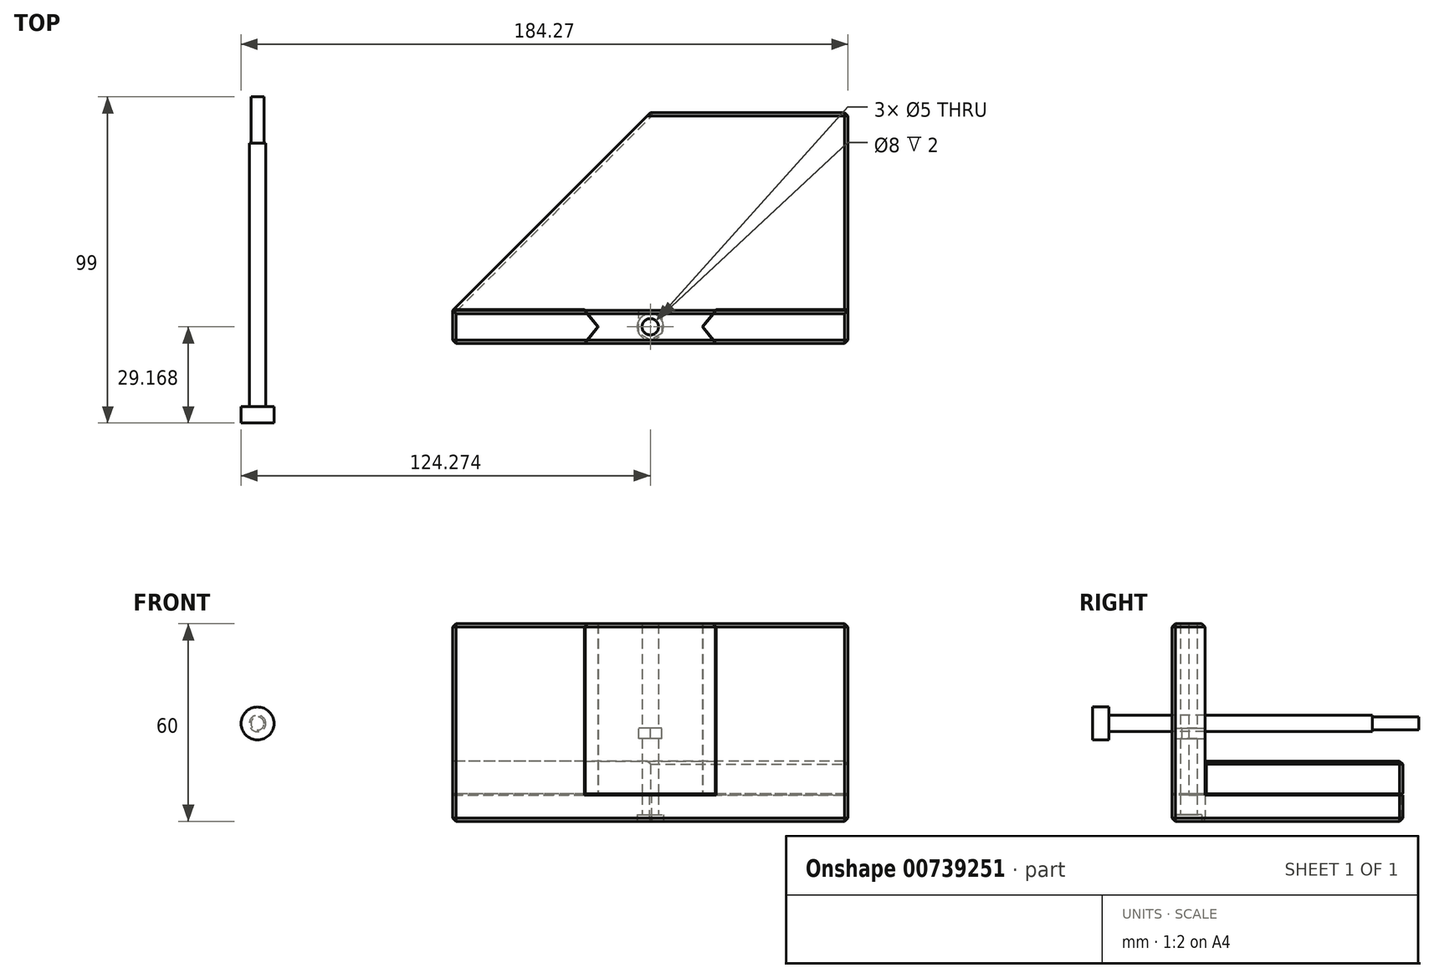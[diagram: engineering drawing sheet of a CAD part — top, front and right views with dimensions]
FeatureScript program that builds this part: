
annotation { "Feature Type Name" : "Feature", "Feature Type Description" : "" }
export const myFeature = defineFeature(function(context is Context, id is Id, definition is map)
    precondition{}
    {
        {
            var Q0;
            Q0=qCreatedBy(makeId("Top.planeOp"),FACE);
            var sketch = newSketch(context, id + "F0", { "sketchPlane" : qUnion([Q0])});
            skLineSegment(sketch, "E0", {"start": v(72.15, 89.17) * mm, "end": v(72.15, 29.17) * mm});
            skLineSegment(sketch, "E1", {"start": v(72.15, 29.17) * mm, "end": v(-47.85, 29.17) * mm});
            skLineSegment(sketch, "E2", {"start": v(-47.85, 29.17) * mm, "end": v(12.15, 89.17) * mm});
            skLineSegment(sketch, "E3", {"start": v(12.15, 89.17) * mm, "end": v(72.15, 89.17) * mm});
            skSolve(sketch);
        }
        {
            var Q0;
            Q0=makeQuery(id+"F0.imprint","IMPRINT",FACE,{"disambiguationData":[TD([[makeQuery(id+"F0.imprint","IMPRINT",EDGE,{"derivedFrom":sQuery(id+"F0.wireOp",EDGE,"E0")}),-1.0]])]});
            extrude(context, id + "F1", {"entities" : qUnion([Q0]), "depth" : 8 * mm, "offsetDistance" : 25 * mm});
        }
        {
            var Q0;
            Q0=makeQuery(id+"F1.opExtrude","CAP_FACE",FACE,{"disambiguationData":[OSD([sQuery(id+"F0.wireOp",EDGE,"E0"),sQuery(id+"F0.wireOp",EDGE,"E1"),sQuery(id+"F0.wireOp",EDGE,"E2"),sQuery(id+"F0.wireOp",EDGE,"E3")])],"isStart":false});
            var sketch = newSketch(context, id + "F2", { "sketchPlane" : qUnion([Q0])});
            skLineSegment(sketch, "E4.0", {"start": v(72.15, 29.17) * mm, "end": v(-47.85, 29.17) * mm});
            skLineSegment(sketch, "E5", {"start": v(72.15, 29.17) * mm, "end": v(72.15, 19.17) * mm});
            skLineSegment(sketch, "E6", {"start": v(72.15, 19.17) * mm, "end": v(-47.85, 19.17) * mm});
            skLineSegment(sketch, "E7", {"start": v(-47.85, 19.17) * mm, "end": v(-47.85, 29.17) * mm});
            skLineSegment(sketch, "E8", {"start": v(12.15, 19.17) * mm, "end": v(12.15, 29.17) * mm, "construction": true});
            skLineSegment(sketch, "E9", {"start": v(-7.85, 29.17) * mm, "end": v(-3.8, 24.17) * mm});
            skLineSegment(sketch, "E10", {"start": v(-3.8, 24.17) * mm, "end": v(-7.85, 19.17) * mm});
            skLineSegment(sketch, "E11.MirrorCS", {"start": v(32.15, 29.17) * mm, "end": v(28.1, 24.17) * mm});
            skLineSegment(sketch, "E12.MirrorCS", {"start": v(28.1, 24.17) * mm, "end": v(32.15, 19.17) * mm});
            skLineSegment(sketch, "E13", {"start": v(-7.85, 29.17) * mm, "end": v(-7.85, 19.17) * mm, "construction": true});
            skSolve(sketch);
        }
        {
            var Q0;
            {var subQ1=sQuery(id+"F2.wireOp",EDGE,"E5");Q0=makeQuery(id+"F2.imprint","IMPRINT",FACE,{"disambiguationData":[TD([[makeQuery(id+"F2.imprint","IMPRINT",EDGE,{"derivedFrom":subQ1}),-1.0]])]});}
            var Q1;
            {var subQ1=sQuery(id+"F2.wireOp",EDGE,"E9");Q1=makeQuery(id+"F2.imprint","IMPRINT",FACE,{"disambiguationData":[TD([[makeQuery(id+"F2.imprint","IMPRINT",EDGE,{"derivedFrom":subQ1}),1.0]])]});}
            var Q2;
            {var subQ1=sQuery(id+"F2.wireOp",EDGE,"E7");Q2=makeQuery(id+"F2.imprint","IMPRINT",FACE,{"disambiguationData":[TD([[makeQuery(id+"F2.imprint","IMPRINT",EDGE,{"derivedFrom":subQ1}),-1.0]])]});}
            var Q3;
            Q3=makeQuery(id+"F1.opExtrude","CAP_FACE",FACE,{"disambiguationData":[OSD([sQuery(id+"F0.wireOp",EDGE,"E0"),sQuery(id+"F0.wireOp",EDGE,"E1"),sQuery(id+"F0.wireOp",EDGE,"E2"),sQuery(id+"F0.wireOp",EDGE,"E3")])],"isStart":true});
            extrude(context, id + "F3", {"entities" : qUnion([Q0, Q1, Q2]), "operationType" : NewBodyOperationType.ADD, "endBound" : BoundingType.UP_TO_SURFACE, "oppositeDirection" : true, "depth" : 25 * mm, "endBoundEntityFace" : qUnion([Q3]), "offsetDistance" : 25 * mm});
        }
        {
            var Q0;
            {var subQ1=sQuery(id+"F2.wireOp",EDGE,"E7");Q0=makeQuery(id+"F2.imprint","IMPRINT",FACE,{"disambiguationData":[TD([[makeQuery(id+"F2.imprint","IMPRINT",EDGE,{"derivedFrom":subQ1}),-1.0]])]});}
            var Q1;
            {var subQ1=sQuery(id+"F2.wireOp",EDGE,"E5");Q1=makeQuery(id+"F2.imprint","IMPRINT",FACE,{"disambiguationData":[TD([[makeQuery(id+"F2.imprint","IMPRINT",EDGE,{"derivedFrom":subQ1}),-1.0]])]});}
            extrude(context, id + "F4", {"entities" : qUnion([Q0, Q1]), "operationType" : NewBodyOperationType.ADD, "depth" : 52 * mm, "offsetDistance" : 25 * mm});
        }
        {
            var Q0;
            {var subQ0=makeQuery(id+"F1.opExtrude","CAP_EDGE",EDGE,{"disambiguationData":[OSD([sQuery(id+"F0.wireOp",EDGE,"E0")])],"isStart":false});Q0=makeQuery(id+"F2.imprint","IMPRINT",FACE,{"disambiguationData":[TD([[makeQuery(id+"F2.imprint","IMPRINT",EDGE,{"derivedFrom":subQ0}),-1.0]])]});}
            cPlane(context, id + "F5", {"entities" : qUnion([Q0]), "cplaneType" : CPlaneType.OFFSET, "offset" : 0.3 * mm, "width" : 150 * mm, "height" : 150 * mm});
        }
        {
            var Q0;
            Q0=qCreatedBy(id+"F5.planeOp",FACE);
            var sketch = newSketch(context, id + "F6", { "sketchPlane" : qUnion([Q0])});
            skLineSegment(sketch, "E14.0", {"start": v(12.15, 89.17) * mm, "end": v(72.15, 89.17) * mm});
            skLineSegment(sketch, "E15.0", {"start": v(-47.85, 29.17) * mm, "end": v(12.15, 89.17) * mm});
            skLineSegment(sketch, "E16.0", {"start": v(72.15, 89.17) * mm, "end": v(72.15, 29.17) * mm});
            skLineSegment(sketch, "E17.0", {"start": v(72.15, 29.17) * mm, "end": v(72.15, 19.17) * mm});
            skLineSegment(sketch, "E18.0", {"start": v(-47.85, 19.17) * mm, "end": v(-47.85, 29.17) * mm});
            skLineSegment(sketch, "E19.0", {"start": v(72.15, 19.17) * mm, "end": v(-47.85, 19.17) * mm});
            skLineSegment(sketch, "E20.0", {"start": v(72.15, 29.17) * mm, "end": v(-47.85, 29.17) * mm, "construction": true});
            skLineSegment(sketch, "E21.0", {"start": v(12.15, 19.17) * mm, "end": v(12.15, 29.17) * mm, "construction": true});
            skLineSegment(sketch, "E22.0", {"start": v(-7.85, 29.17) * mm, "end": v(-7.85, 19.17) * mm, "construction": true});
            skLineSegment(sketch, "E23.0", {"start": v(-7.85, 29.17) * mm, "end": v(-3.8, 24.17) * mm, "construction": true});
            skLineSegment(sketch, "E24.0", {"start": v(-3.8, 24.17) * mm, "end": v(-7.85, 19.17) * mm, "construction": true});
            skLineSegment(sketch, "E25.0", {"start": v(32.15, 29.17) * mm, "end": v(28.1, 24.17) * mm, "construction": true});
            skLineSegment(sketch, "E26.0", {"start": v(28.1, 24.17) * mm, "end": v(32.15, 19.17) * mm, "construction": true});
            skLineSegment(sketch, "E27", {"start": v(-47.55, 29.47) * mm, "end": v(72.15, 29.47) * mm});
            skLineSegment(sketch, "E28.0", {"start": v(27.91, 24.17) * mm, "end": v(31.96, 19.17) * mm});
            skLineSegment(sketch, "E28.1", {"start": v(32.2, 29.47) * mm, "end": v(27.91, 24.17) * mm});
            skLineSegment(sketch, "E29.MirrorCS", {"start": v(-7.9, 29.47) * mm, "end": v(-3.6, 24.17) * mm});
            skLineSegment(sketch, "E30.MirrorCS", {"start": v(-3.6, 24.17) * mm, "end": v(-7.65, 19.17) * mm});
            skLineSegment(sketch, "E31", {"start": v(31.96, 29.17) * mm, "end": v(-7.65, 29.17) * mm});
            skSolve(sketch);
        }
        {
            var Q0;
            {var subQ3=sQuery(id+"F6.wireOp",EDGE,"E28.0");Q0=makeQuery(id+"F6.imprint","IMPRINT",FACE,{"disambiguationData":[TD([[makeQuery(id+"F6.imprint","IMPRINT",EDGE,{"derivedFrom":subQ3}),-1.0]])]});}
            var Q1;
            {var subQ5=sQuery(id+"F6.wireOp",EDGE,"E31");Q1=makeQuery(id+"F6.imprint","IMPRINT",FACE,{"disambiguationData":[TD([[makeQuery(id+"F6.imprint","IMPRINT",EDGE,{"derivedFrom":subQ5}),-1.0]])]});}
            var Q2;
            Q2=makeQuery(id+"F4.opExtrude","CAP_FACE",FACE,{"disambiguationData":[OSD([sQuery(id+"F2.wireOp",EDGE,"E4.0"),sQuery(id+"F2.wireOp",EDGE,"E6"),sQuery(id+"F2.wireOp",EDGE,"E7"),sQuery(id+"F2.wireOp",EDGE,"E9"),sQuery(id+"F2.wireOp",EDGE,"E10")])],"isStart":false});
            extrude(context, id + "F7", {"entities" : qUnion([Q0, Q1]), "depth" : 10 * mm, "endBoundEntityFace" : qUnion([Q2]), "offsetDistance" : 25 * mm});
        }
        {
            var Q0;
            Q0=makeQuery(id+"F7.opExtrude","SWEPT_FACE",FACE,{"disambiguationData":[OSD([sQuery(id+"F6.wireOp",EDGE,"E27")])]});
            var sketch = newSketch(context, id + "F8", { "sketchPlane" : qUnion([Q0])});
            skLineSegment(sketch, "E32.0", {"start": v(-72.15, 60) * mm, "end": v(-72.15, 8) * mm, "construction": true});
            skLineSegment(sketch, "E33.0", {"start": v(47.85, 60) * mm, "end": v(47.85, 8) * mm, "construction": true});
            skLineSegment(sketch, "E34.0", {"start": v(7.9, 8.3) * mm, "end": v(-32.2, 8.3) * mm, "construction": true});
            skLineSegment(sketch, "E35", {"start": v(-72.15, 18.3) * mm, "end": v(47.85, 18.3) * mm});
            skLineSegment(sketch, "E36", {"start": v(-72.15, 8.3) * mm, "end": v(47.85, 8.3) * mm});
            skLineSegment(sketch, "E37", {"start": v(-72.15, 8.3) * mm, "end": v(-72.15, 18.3) * mm});
            skLineSegment(sketch, "E38", {"start": v(47.85, 8.3) * mm, "end": v(47.85, 18.3) * mm});
            skSolve(sketch);
        }
        {
            var Q0;
            Q0 = qSketchRegion(id + "F8", true);
            var Q1;
            Q1=makeQuery(id+"F1.opExtrude","SWEPT_FACE",FACE,{"disambiguationData":[OSD([sQuery(id+"F0.wireOp",EDGE,"E3")])]});
            extrude(context, id + "F9", {"entities" : qUnion([Q0]), "operationType" : NewBodyOperationType.ADD, "endBound" : BoundingType.UP_TO_SURFACE, "depth" : 25 * mm, "endBoundEntityFace" : qUnion([Q1]), "offsetDistance" : 25 * mm});
        }
        {
            var Q0;
            Q0=makeQuery(id+"F3.boolean.opBoolean","MERGE",FACE,{"derivedFrom":[makeQuery(id+"F1.opExtrude","CAP_FACE",FACE,{"disambiguationData":[OSD([sQuery(id+"F0.wireOp",EDGE,"E0"),sQuery(id+"F0.wireOp",EDGE,"E1"),sQuery(id+"F0.wireOp",EDGE,"E2"),sQuery(id+"F0.wireOp",EDGE,"E3")])],"isStart":true}),makeQuery(id+"F3.opExtrude","CAP_FACE",FACE,{"disambiguationData":[OSD([sQuery(id+"F2.wireOp",EDGE,"E4.0"),sQuery(id+"F2.wireOp",EDGE,"E5"),sQuery(id+"F2.wireOp",EDGE,"E6"),sQuery(id+"F2.wireOp",EDGE,"E7")])],"isStart":false})]});
            extrude(context, id + "F10", {"entities" : qUnion([Q0]), "operationType" : NewBodyOperationType.INTERSECT, "endBound" : BoundingType.THROUGH_ALL, "oppositeDirection" : true, "depth" : 30.5 * mm, "offsetDistance" : 25 * mm});
        }
        {
            var Q0;
            {var subQ4=sQuery(id+"F6.wireOp",EDGE,"E28.0");Q0=makeQuery(id+"F6.imprint","IMPRINT",FACE,{"disambiguationData":[TD([[makeQuery(id+"F6.imprint","IMPRINT",EDGE,{"derivedFrom":subQ4}),-1.0]])]});}
            var Q1;
            Q1=makeQuery(id+"F4.opExtrude","CAP_FACE",FACE,{"disambiguationData":[OSD([sQuery(id+"F2.wireOp",EDGE,"E4.0"),sQuery(id+"F2.wireOp",EDGE,"E5"),sQuery(id+"F2.wireOp",EDGE,"E6"),sQuery(id+"F2.wireOp",EDGE,"E11.MirrorCS"),sQuery(id+"F2.wireOp",EDGE,"E12.MirrorCS")])],"isStart":false});
            extrude(context, id + "F11", {"entities" : qUnion([Q0]), "operationType" : NewBodyOperationType.ADD, "endBound" : BoundingType.UP_TO_SURFACE, "depth" : 25 * mm, "endBoundEntityFace" : qUnion([Q1]), "offsetDistance" : 25 * mm});
        }
        {
            var Q0;
            Q0=makeQuery(id+"F3.boolean.opBoolean","MERGE",FACE,{"derivedFrom":[makeQuery(id+"F1.opExtrude","CAP_FACE",FACE,{"disambiguationData":[OSD([sQuery(id+"F0.wireOp",EDGE,"E0"),sQuery(id+"F0.wireOp",EDGE,"E1"),sQuery(id+"F0.wireOp",EDGE,"E2"),sQuery(id+"F0.wireOp",EDGE,"E3")])],"isStart":true}),makeQuery(id+"F3.opExtrude","CAP_FACE",FACE,{"disambiguationData":[OSD([sQuery(id+"F2.wireOp",EDGE,"E4.0"),sQuery(id+"F2.wireOp",EDGE,"E5"),sQuery(id+"F2.wireOp",EDGE,"E6"),sQuery(id+"F2.wireOp",EDGE,"E7")])],"isStart":false})]});
            var sketch = newSketch(context, id + "F12", { "sketchPlane" : qUnion([Q0])});
            skPoint(sketch, "E39.0", {"position": v(12.15, -24.17) * mm});
            skCircle(sketch, "E40", {"center": v(12.15, -24.17) * mm, "radius": 2.5 * mm});
            skCircle(sketch, "E41", {"center": v(12.15, -24.17) * mm, "radius": 4 * mm});
            skSolve(sketch);
        }
        {
            var Q0;
            {var subQ4=sQuery(id+"F6.wireOp",EDGE,"E28.0");Q0=makeQuery(id+"F6.imprint","IMPRINT",FACE,{"disambiguationData":[TD([[makeQuery(id+"F6.imprint","IMPRINT",EDGE,{"derivedFrom":subQ4}),-1.0]])]});}
            var sketch = newSketch(context, id + "F13", { "sketchPlane" : qUnion([Q0])});
            skPoint(sketch, "E42.0", {"position": v(12.15, 24.17) * mm});
            skCircle(sketch, "E43", {"center": v(12.15, 24.17) * mm, "radius": 2 * mm});
            skCircle(sketch, "E44", {"center": v(12.15, 24.17) * mm, "radius": 2.5 * mm});
            skSolve(sketch);
        }
        {
            var Q0;
            Q0=makeQuery(id+"F10.boolean.opBoolean","INTERSECT",EDGE,{"derivedFrom":[makeQuery(id+"F9.boolean.opBoolean","MERGE",FACE,{"derivedFrom":[makeQuery(id+"F7.opExtrude","CAP_FACE",FACE,{"disambiguationData":[OSD([sQuery(id+"F6.wireOp",EDGE,"E19.0"),sQuery(id+"F6.wireOp",EDGE,"E27"),sQuery(id+"F6.wireOp",EDGE,"E28.0"),sQuery(id+"F6.wireOp",EDGE,"E28.1"),sQuery(id+"F6.wireOp",EDGE,"E29.MirrorCS"),sQuery(id+"F6.wireOp",EDGE,"E30.MirrorCS")])],"isStart":false}),makeQuery(id+"F9.opExtrude","SWEPT_FACE",FACE,{"disambiguationData":[OSD([sQuery(id+"F8.wireOp",EDGE,"E35")])]})]}),makeQuery(id+"F10.boolean.toolComplement.opBoolean","COPY",FACE,{"derivedFrom":makeQuery(id+"F10.opExtrude","SWEPT_FACE",FACE,{"disambiguationData":[OSD([sQuery(id+"F0.wireOp",EDGE,"E2")])]})})]});
            var Q1;
            {var subQ0=sQuery(id+"F2.wireOp",EDGE,"E6");var subQ1=sQuery(id+"F2.wireOp",EDGE,"E5");Q1=makeQuery(id+"F4.boolean.opBoolean","MERGE",EDGE,{"derivedFrom":[makeQuery(id+"F3.opExtrude","SWEPT_EDGE",EDGE,{"disambiguationData":[OSD([subQ1,subQ0])]}),makeQuery(id+"F4.opExtrude","SWEPT_EDGE",EDGE,{"disambiguationData":[OSD([subQ1,subQ0])]})]});}
            var Q2;
            Q2=makeQuery(id+"F3.boolean.opBoolean","MERGE",EDGE,{"derivedFrom":[makeQuery(id+"F1.opExtrude","CAP_EDGE",EDGE,{"disambiguationData":[OSD([sQuery(id+"F0.wireOp",EDGE,"E0")])],"isStart":true}),makeQuery(id+"F3.opExtrude","CAP_EDGE",EDGE,{"disambiguationData":[OSD([sQuery(id+"F2.wireOp",EDGE,"E5")])],"isStart":false})]});
            var Q3;
            Q3=makeQuery(id+"F1.opExtrude","CAP_EDGE",EDGE,{"disambiguationData":[OSD([sQuery(id+"F0.wireOp",EDGE,"E3")])],"isStart":true});
            var Q4;
            Q4=makeQuery(id+"F1.opExtrude","CAP_EDGE",EDGE,{"disambiguationData":[OSD([sQuery(id+"F0.wireOp",EDGE,"E2")])],"isStart":true});
            var Q5;
            Q5=makeQuery(id+"F3.opExtrude","CAP_EDGE",EDGE,{"disambiguationData":[OSD([sQuery(id+"F2.wireOp",EDGE,"E6")])],"isStart":false});
            var Q6;
            Q6=makeQuery(id+"F3.opExtrude","CAP_EDGE",EDGE,{"disambiguationData":[OSD([sQuery(id+"F2.wireOp",EDGE,"E7")])],"isStart":false});
            var Q7;
            {var subQ0=sQuery(id+"F2.wireOp",EDGE,"E7");var subQ1=sQuery(id+"F2.wireOp",EDGE,"E6");Q7=makeQuery(id+"F4.boolean.opBoolean","MERGE",EDGE,{"derivedFrom":[makeQuery(id+"F3.opExtrude","SWEPT_EDGE",EDGE,{"disambiguationData":[OSD([subQ1,subQ0])]}),makeQuery(id+"F4.opExtrude","SWEPT_EDGE",EDGE,{"disambiguationData":[OSD([subQ1,subQ0])]})]});}
            var Q8;
            Q8=makeQuery(id+"F4.opExtrude","CAP_EDGE",EDGE,{"disambiguationData":[OSD([sQuery(id+"F2.wireOp",EDGE,"E7")])],"isStart":false});
            var Q9;
            {var subQ0=sQuery(id+"F2.wireOp",EDGE,"E6");Q9=makeQuery(id+"F4.opExtrude","CAP_EDGE",EDGE,{"disambiguationData":[OSD([subQ0]),TDD([makeQuery(id+"F2.imprint","IMPRINT",EDGE,{"disambiguationData":[TD([[makeQuery(id+"F2.imprint","INTERSECT",VERTEX,{"derivedFrom":[subQ0,sQuery(id+"F2.wireOp",EDGE,"E7")]}),1.0]])],"derivedFrom":subQ0})])],"isStart":false});}
            var Q10;
            {var subQ0=sQuery(id+"F2.wireOp",EDGE,"E4.0");Q10=makeQuery(id+"F4.opExtrude","CAP_EDGE",EDGE,{"disambiguationData":[OSD([subQ0]),TDD([makeQuery(id+"F2.imprint","IMPRINT",EDGE,{"disambiguationData":[TD([[makeQuery(id+"F2.imprint","INTERSECT",VERTEX,{"derivedFrom":[subQ0,sQuery(id+"F2.wireOp",EDGE,"E9")]}),-1.0]])],"derivedFrom":subQ0})])],"isStart":false});}
            var Q11;
            {var subQ0=sQuery(id+"F2.wireOp",EDGE,"E6");Q11=makeQuery(id+"F4.opExtrude","CAP_EDGE",EDGE,{"disambiguationData":[OSD([subQ0]),TDD([makeQuery(id+"F2.imprint","IMPRINT",EDGE,{"disambiguationData":[TD([[makeQuery(id+"F2.imprint","INTERSECT",VERTEX,{"derivedFrom":[sQuery(id+"F2.wireOp",EDGE,"E5"),subQ0]}),-1.0]])],"derivedFrom":subQ0})])],"isStart":false});}
            var Q12;
            {var subQ0=sQuery(id+"F2.wireOp",EDGE,"E4.0");Q12=makeQuery(id+"F4.opExtrude","CAP_EDGE",EDGE,{"disambiguationData":[OSD([subQ0]),TDD([makeQuery(id+"F2.imprint","IMPRINT",EDGE,{"disambiguationData":[TD([[makeQuery(id+"F2.imprint","INTERSECT",VERTEX,{"derivedFrom":[subQ0,sQuery(id+"F2.wireOp",EDGE,"E11.MirrorCS")]}),1.0]])],"derivedFrom":subQ0})])],"isStart":false});}
            var Q13;
            Q13=makeQuery(id+"F4.opExtrude","CAP_EDGE",EDGE,{"disambiguationData":[OSD([sQuery(id+"F2.wireOp",EDGE,"E5")])],"isStart":false});
            var Q14;
            Q14=makeQuery(id+"F11.opExtrude","CAP_EDGE",EDGE,{"disambiguationData":[OSD([sQuery(id+"F6.wireOp",EDGE,"E31")])],"isStart":false});
            var Q15;
            Q15=makeQuery(id+"F11.opExtrude","CAP_EDGE",EDGE,{"disambiguationData":[OSD([sQuery(id+"F6.wireOp",EDGE,"E19.0")])],"isStart":false});
            var Q16;
            Q16=makeQuery(id+"F9.opExtrude","SWEPT_EDGE",EDGE,{"disambiguationData":[OSD([sQuery(id+"F8.wireOp",EDGE,"E35"),sQuery(id+"F8.wireOp",EDGE,"E37")])]});
            var Q17;
            Q17=makeQuery(id+"F9.opExtrude","CAP_EDGE",EDGE,{"disambiguationData":[OSD([sQuery(id+"F8.wireOp",EDGE,"E35")])],"isStart":false});
            var Q18;
            Q18=makeQuery(id+"F9.opExtrude","CAP_EDGE",EDGE,{"disambiguationData":[OSD([sQuery(id+"F8.wireOp",EDGE,"E37")])],"isStart":false});
            var Q19;
            Q19=makeQuery(id+"F1.opExtrude","SWEPT_EDGE",EDGE,{"disambiguationData":[OSD([sQuery(id+"F0.wireOp",EDGE,"E0"),sQuery(id+"F0.wireOp",EDGE,"E3")])]});
            var Q20;
            Q20=makeQuery(id+"F1.opExtrude","SWEPT_EDGE",EDGE,{"disambiguationData":[OSD([sQuery(id+"F0.wireOp",EDGE,"E2"),sQuery(id+"F0.wireOp",EDGE,"E3")])]});
            var Q21;
            Q21=makeQuery(id+"F10.boolean.opBoolean","COPY",EDGE,{"derivedFrom":makeQuery(id+"F10.boolean.toolComplement.opBoolean","COPY",EDGE,{"derivedFrom":makeQuery(id+"F10.opExtrude","SWEPT_EDGE",EDGE,{"disambiguationData":[OSD([sQuery(id+"F0.wireOp",EDGE,"E2"),sQuery(id+"F0.wireOp",EDGE,"E3")])]})})});
            chamfer(context, id + "F14", {"entities" : qUnion([Q0, Q1, Q2, Q3, Q4, Q5, Q6, Q7, Q8, Q9, Q10, Q11, Q12, Q13, Q14, Q15, Q16, Q17, Q18, Q19, Q20, Q21]), "width" : 1 * mm, "tangentPropagation" : true});
        }
        {
            var Q0;
            {var subQ4=sQuery(id+"F6.wireOp",EDGE,"E28.0");Q0=makeQuery(id+"F6.imprint","IMPRINT",FACE,{"disambiguationData":[TD([[makeQuery(id+"F6.imprint","IMPRINT",EDGE,{"derivedFrom":subQ4}),-1.0]])]});}
            cPlane(context, id + "F15", {"entities" : qUnion([Q0]), "cplaneType" : CPlaneType.OFFSET, "offset" : 20 * mm, "width" : 150 * mm, "height" : 150 * mm});
        }
        {
            var Q0;
            Q0=qCreatedBy(id+"F15.planeOp",FACE);
            var sketch = newSketch(context, id + "F16", { "sketchPlane" : qUnion([Q0])});
            skPoint(sketch, "E45.0", {"position": v(12.15, 24.17) * mm});
            skCircle(sketch, "E46.cCircle", {"center": v(12.15, 24.17) * mm, "radius": 3.5 * mm, "construction": true});
            skLineSegment(sketch, "E46.0", {"start": v(12.15, 28.2) * mm, "end": v(15.65, 26.19) * mm});
            skLineSegment(sketch, "E46.1", {"start": v(15.65, 29.17) * mm, "end": v(15.65, 22.15) * mm});
            skLineSegment(sketch, "E46.2", {"start": v(15.65, 22.15) * mm, "end": v(12.15, 20.13) * mm});
            skLineSegment(sketch, "E46.3", {"start": v(12.15, 20.13) * mm, "end": v(8.65, 22.15) * mm});
            skLineSegment(sketch, "E46.4", {"start": v(8.65, 22.15) * mm, "end": v(8.65, 29.17) * mm});
            skLineSegment(sketch, "E46.5", {"start": v(8.65, 26.19) * mm, "end": v(12.15, 28.2) * mm});
            skPoint(sketch, "E46.0.midPoint", {"position": v(13.9, 27.2) * mm});
            skLineSegment(sketch, "E47.0", {"start": v(31.96, 29.17) * mm, "end": v(-7.65, 29.17) * mm});
            skSolve(sketch);
        }
        {
            var Q0;
            {var subQ5=sQuery(id+"F16.wireOp",EDGE,"E46.0");Q0=makeQuery(id+"F16.imprint","IMPRINT",FACE,{"disambiguationData":[TD([[makeQuery(id+"F16.imprint","IMPRINT",EDGE,{"derivedFrom":subQ5}),1.0]])]});}
            var Q1;
            {var subQ3=sQuery(id+"F16.wireOp",EDGE,"E46.0");Q1=makeQuery(id+"F16.imprint","IMPRINT",FACE,{"disambiguationData":[TD([[makeQuery(id+"F16.imprint","IMPRINT",EDGE,{"derivedFrom":subQ3}),-1.0]])]});}
            extrude(context, id + "F17", {"entities" : qUnion([Q0, Q1]), "operationType" : NewBodyOperationType.REMOVE, "oppositeDirection" : true, "depth" : 3.2 * mm, "offsetDistance" : 25 * mm});
        }
        {
            var Q0;
            Q0=makeQuery(id+"F13.imprint","IMPRINT",FACE,{"disambiguationData":[TD([[makeQuery(id+"F13.imprint","IMPRINT",EDGE,{"derivedFrom":sQuery(id+"F13.wireOp",EDGE,"E43")}),-1.0]])]});
            var Q1;
            Q1=makeQuery(id+"F13.imprint","IMPRINT",FACE,{"disambiguationData":[TD([[makeQuery(id+"F13.imprint","IMPRINT",EDGE,{"derivedFrom":sQuery(id+"F13.wireOp",EDGE,"E43")}),1.0]])]});
            extrude(context, id + "F18", {"entities" : qUnion([Q0, Q1]), "operationType" : NewBodyOperationType.REMOVE, "depth" : 10 * mm, "offsetDistance" : 25 * mm});
        }
        {
            var Q0;
            Q0=makeQuery(id+"F13.imprint","IMPRINT",FACE,{"disambiguationData":[TD([[makeQuery(id+"F13.imprint","IMPRINT",EDGE,{"derivedFrom":sQuery(id+"F13.wireOp",EDGE,"E43")}),1.0]])]});
            extrude(context, id + "F19", {"entities" : qUnion([Q0]), "operationType" : NewBodyOperationType.REMOVE, "depth" : 25 * mm, "offsetDistance" : 10 * mm, "offsetOppositeDirection" : true});
        }
        {
            var Q0;
            Q0=makeQuery(id+"F10.boolean.opBoolean","INTERSECT",EDGE,{"derivedFrom":[makeQuery(id+"F9.boolean.opBoolean","MERGE",FACE,{"derivedFrom":[makeQuery(id+"F7.opExtrude","CAP_FACE",FACE,{"disambiguationData":[OSD([sQuery(id+"F6.wireOp",EDGE,"E19.0"),sQuery(id+"F6.wireOp",EDGE,"E27"),sQuery(id+"F6.wireOp",EDGE,"E28.0"),sQuery(id+"F6.wireOp",EDGE,"E28.1"),sQuery(id+"F6.wireOp",EDGE,"E29.MirrorCS"),sQuery(id+"F6.wireOp",EDGE,"E30.MirrorCS")])],"isStart":true}),makeQuery(id+"F9.opExtrude","SWEPT_FACE",FACE,{"disambiguationData":[OSD([sQuery(id+"F8.wireOp",EDGE,"E36")])]})]}),makeQuery(id+"F10.boolean.toolComplement.opBoolean","COPY",FACE,{"derivedFrom":makeQuery(id+"F10.opExtrude","SWEPT_FACE",FACE,{"disambiguationData":[OSD([sQuery(id+"F0.wireOp",EDGE,"E2")])]})})]});
            var Q1;
            {var subQ1=sQuery(id+"F8.wireOp",EDGE,"E36");var subQ2=sQuery(id+"F6.wireOp",EDGE,"E29.MirrorCS");Q1=makeQuery(id+"F9.boolean.opBoolean","SPLIT",EDGE,{"disambiguationData":[TD([makeQuery(id+"F7.opExtrude","SWEPT_FACE",FACE,{"disambiguationData":[OSD([subQ2])]})])],"derivedFrom":makeQuery(id+"F9.opExtrude","CAP_EDGE",EDGE,{"disambiguationData":[OSD([subQ1])],"isStart":true})});}
            var Q2;
            Q2=makeQuery(id+"F7.opExtrude","CAP_EDGE",EDGE,{"disambiguationData":[OSD([sQuery(id+"F6.wireOp",EDGE,"E29.MirrorCS")])],"isStart":true});
            var Q3;
            Q3=makeQuery(id+"F7.opExtrude","CAP_EDGE",EDGE,{"disambiguationData":[OSD([sQuery(id+"F6.wireOp",EDGE,"E30.MirrorCS")])],"isStart":true});
            var Q4;
            Q4=makeQuery(id+"F7.opExtrude","CAP_EDGE",EDGE,{"disambiguationData":[OSD([sQuery(id+"F6.wireOp",EDGE,"E19.0")])],"isStart":true});
            var Q5;
            Q5=makeQuery(id+"F7.opExtrude","CAP_EDGE",EDGE,{"disambiguationData":[OSD([sQuery(id+"F6.wireOp",EDGE,"E28.0")])],"isStart":true});
            var Q6;
            Q6=makeQuery(id+"F7.opExtrude","CAP_EDGE",EDGE,{"disambiguationData":[OSD([sQuery(id+"F6.wireOp",EDGE,"E28.1")])],"isStart":true});
            var Q7;
            {var subQ1=sQuery(id+"F8.wireOp",EDGE,"E36");var subQ2=sQuery(id+"F6.wireOp",EDGE,"E28.1");Q7=makeQuery(id+"F9.boolean.opBoolean","SPLIT",EDGE,{"disambiguationData":[TD([makeQuery(id+"F7.opExtrude","SWEPT_FACE",FACE,{"disambiguationData":[OSD([subQ2])]})])],"derivedFrom":makeQuery(id+"F9.opExtrude","CAP_EDGE",EDGE,{"disambiguationData":[OSD([subQ1])],"isStart":true})});}
            var Q8;
            Q8=makeQuery(id+"F9.opExtrude","SWEPT_EDGE",EDGE,{"disambiguationData":[OSD([sQuery(id+"F8.wireOp",EDGE,"E36"),sQuery(id+"F8.wireOp",EDGE,"E37")])]});
            var Q9;
            Q9=makeQuery(id+"F9.opExtrude","CAP_EDGE",EDGE,{"disambiguationData":[OSD([sQuery(id+"F8.wireOp",EDGE,"E36")])],"isStart":false});
            fillet(context, id + "F20", {"entities" : qUnion([Q0, Q1, Q2, Q3, Q4, Q5, Q6, Q7, Q8, Q9]), "radius" : 0.2 * mm, "tangentPropagation" : true, "allowEdgeOverflow" : false});
        }
        {
            var Q0;
            Q0=makeQuery(id+"F12.imprint","IMPRINT",FACE,{"disambiguationData":[TD([[makeQuery(id+"F12.imprint","IMPRINT",EDGE,{"derivedFrom":sQuery(id+"F12.wireOp",EDGE,"E40")}),1.0]])]});
            extrude(context, id + "F21", {"entities" : qUnion([Q0]), "operationType" : NewBodyOperationType.REMOVE, "endBound" : BoundingType.THROUGH_ALL, "oppositeDirection" : true, "depth" : 25 * mm, "offsetDistance" : 25 * mm});
        }
        {
            var Q0;
            Q0=makeQuery(id+"F12.imprint","IMPRINT",FACE,{"disambiguationData":[TD([[makeQuery(id+"F12.imprint","IMPRINT",EDGE,{"derivedFrom":sQuery(id+"F12.wireOp",EDGE,"E40")}),-1.0]])]});
            extrude(context, id + "F22", {"entities" : qUnion([Q0]), "operationType" : NewBodyOperationType.REMOVE, "oppositeDirection" : true, "depth" : 2 * mm, "offsetDistance" : 25 * mm});
        }
        {
            var Q0;
            Q0=qCreatedBy(makeId("Front.planeOp"),FACE);
            var sketch = newSketch(context, id + "F23", { "sketchPlane" : qUnion([Q0])});
            skCircle(sketch, "E48", {"center": v(-107.12, 29.71) * mm, "radius": 2.5 * mm});
            skCircle(sketch, "E49", {"center": v(-107.12, 29.71) * mm, "radius": 5 * mm});
            skSolve(sketch);
        }
        {
            var Q0;
            Q0=makeQuery(id+"F23.imprint","IMPRINT",FACE,{"disambiguationData":[TD([[makeQuery(id+"F23.imprint","IMPRINT",EDGE,{"derivedFrom":sQuery(id+"F23.wireOp",EDGE,"E48")}),1.0]])]});
            extrude(context, id + "F24", {"entities" : qUnion([Q0]), "oppositeDirection" : true, "depth" : 80 * mm, "offsetDistance" : 25 * mm});
        }
        {
            var Q0;
            Q0 = qSketchRegion(id + "F23", true);
            var Q1;
            Q1=makeQuery(id+"F23.imprint","IMPRINT",FACE,{"disambiguationData":[TD([[makeQuery(id+"F23.imprint","IMPRINT",EDGE,{"derivedFrom":sQuery(id+"F23.wireOp",EDGE,"E48")}),1.0]])]});
            extrude(context, id + "F25", {"entities" : qUnion([Q0, Q1]), "operationType" : NewBodyOperationType.ADD, "depth" : 5 * mm, "offsetDistance" : 25 * mm});
        }
        {
            var Q0;
            Q0=makeQuery(id+"F24.opExtrude","CAP_FACE",FACE,{"disambiguationData":[OSD([sQuery(id+"F23.wireOp",EDGE,"E48")])],"isStart":false});
            var sketch = newSketch(context, id + "F26", { "sketchPlane" : qUnion([Q0])});
            skCircle(sketch, "E50", {"center": v(107.12, 29.71) * mm, "radius": 2 * mm});
            skSolve(sketch);
        }
        {
            var Q0;
            Q0=makeQuery(id+"F26.imprint","IMPRINT",FACE,{"disambiguationData":[TD([[makeQuery(id+"F26.imprint","IMPRINT",EDGE,{"derivedFrom":sQuery(id+"F26.wireOp",EDGE,"E50")}),1.0]])]});
            extrude(context, id + "F27", {"entities" : qUnion([Q0]), "operationType" : NewBodyOperationType.ADD, "depth" : 14 * mm, "offsetDistance" : 25 * mm});
        }
    });
